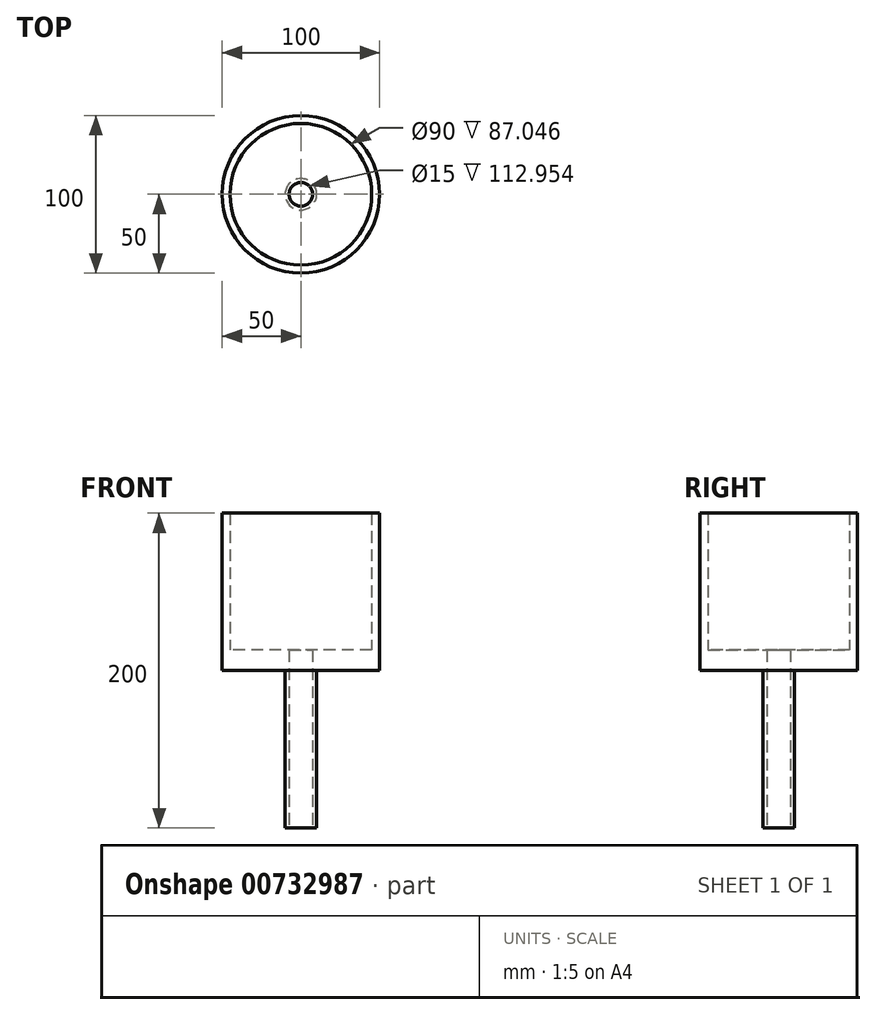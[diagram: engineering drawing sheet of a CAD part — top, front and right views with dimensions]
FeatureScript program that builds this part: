
annotation { "Feature Type Name" : "Feature", "Feature Type Description" : "" }
export const myFeature = defineFeature(function(context is Context, id is Id, definition is map)
    precondition{}
    {
        {
            var Q0;
            Q0=qCreatedBy(makeId("Top.planeOp"),FACE);
            var sketch = newSketch(context, id + "F0", { "sketchPlane" : qUnion([Q0])});
            skCircle(sketch, "E0", {"center": v(0, 0) * mm, "radius": 50 * mm});
            skCircle(sketch, "E1", {"center": v(0, 0) * mm, "radius": 45 * mm});
            skSolve(sketch);
        }
        {
            var Q0;
            Q0 = qSketchRegion(id + "F0", true);
            extrude(context, id + "F1", {"entities" : qUnion([Q0]), "depth" : 100 * mm, "offsetDistance" : 25.4 * mm});
        }
        {
            var Q0;
            Q0=makeQuery(id+"F1.opExtrude","CAP_FACE",FACE,{"disambiguationData":[OSD([sQuery(id+"F0.wireOp",EDGE,"E0"),sQuery(id+"F0.wireOp",EDGE,"E1")])],"isStart":true});
            var sketch = newSketch(context, id + "F2", { "sketchPlane" : qUnion([Q0])});
            skCircle(sketch, "E2", {"center": v(0, 0) * mm, "radius": 45 * mm});
            skSolve(sketch);
        }
        {
            var Q0;
            Q0 = qSketchRegion(id + "F2", true);
            extrude(context, id + "F3", {"entities" : qUnion([Q0]), "operationType" : NewBodyOperationType.ADD, "oppositeDirection" : true, "depth" : 12.95 * mm, "offsetDistance" : 25.4 * mm});
        }
        {
            var Q0;
            Q0=makeQuery(id+"F3.boolean.opBoolean","MERGE",FACE,{"derivedFrom":[makeQuery(id+"F1.opExtrude","CAP_FACE",FACE,{"disambiguationData":[OSD([sQuery(id+"F0.wireOp",EDGE,"E0"),sQuery(id+"F0.wireOp",EDGE,"E1")])],"isStart":true}),makeQuery(id+"F3.opExtrude","CAP_FACE",FACE,{"disambiguationData":[OSD([sQuery(id+"F2.wireOp",EDGE,"E2")])],"isStart":true})]});
            var sketch = newSketch(context, id + "F4", { "sketchPlane" : qUnion([Q0])});
            skCircle(sketch, "E3", {"center": v(0, 0) * mm, "radius": 7.5 * mm});
            skSolve(sketch);
        }
        {
            var Q0;
            Q0 = qSketchRegion(id + "F4", true);
            extrude(context, id + "F5", {"entities" : qUnion([Q0]), "operationType" : NewBodyOperationType.REMOVE, "endBound" : BoundingType.UP_TO_NEXT, "oppositeDirection" : true, "depth" : 25.4 * mm, "offsetDistance" : 25.4 * mm});
        }
        {
            var Q0;
            Q0=makeQuery(id+"F3.boolean.opBoolean","MERGE",FACE,{"derivedFrom":[makeQuery(id+"F1.opExtrude","CAP_FACE",FACE,{"disambiguationData":[OSD([sQuery(id+"F0.wireOp",EDGE,"E0"),sQuery(id+"F0.wireOp",EDGE,"E1")])],"isStart":true}),makeQuery(id+"F3.opExtrude","CAP_FACE",FACE,{"disambiguationData":[OSD([sQuery(id+"F2.wireOp",EDGE,"E2")])],"isStart":true})]});
            var sketch = newSketch(context, id + "F6", { "sketchPlane" : qUnion([Q0])});
            skCircle(sketch, "E4", {"center": v(0, 0) * mm, "radius": 10 * mm});
            skCircle(sketch, "E5", {"center": v(0, 0) * mm, "radius": 7.5 * mm});
            skSolve(sketch);
        }
        {
            var Q0;
            Q0 = qSketchRegion(id + "F6", true);
            extrude(context, id + "F7", {"entities" : qUnion([Q0]), "operationType" : NewBodyOperationType.ADD, "depth" : 100 * mm, "offsetDistance" : 25 * mm});
        }
    });
